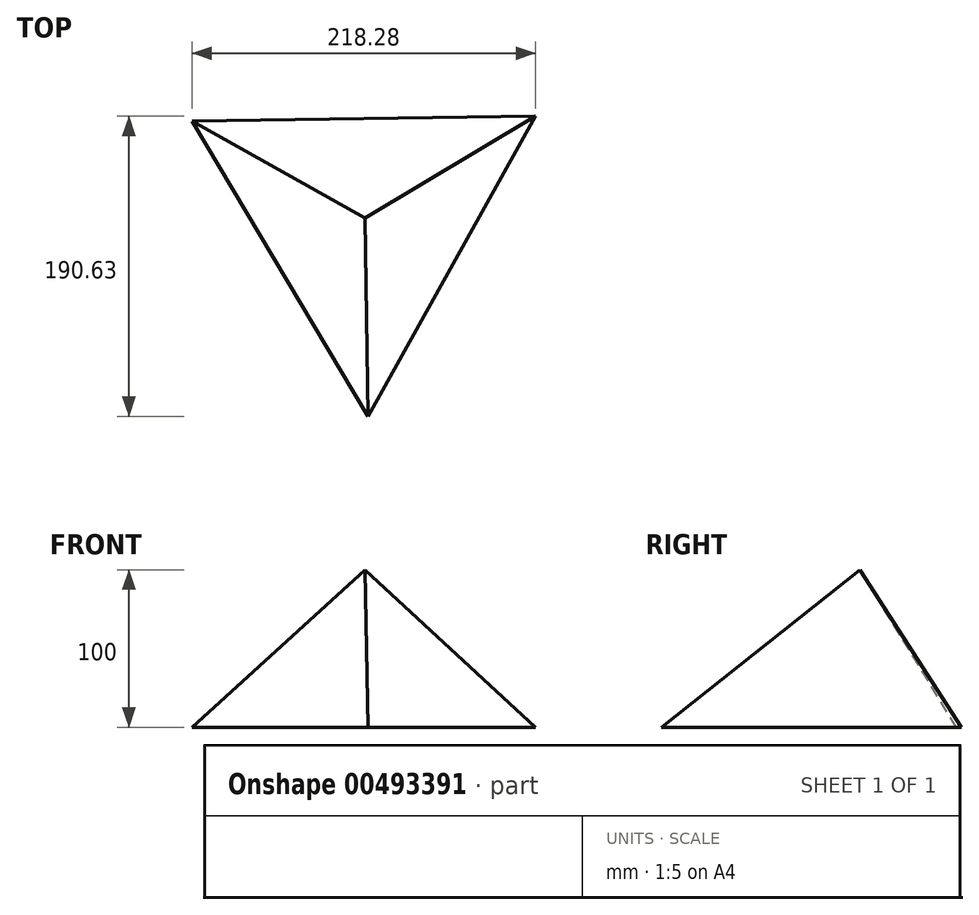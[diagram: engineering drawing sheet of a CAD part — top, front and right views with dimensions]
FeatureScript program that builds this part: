
annotation { "Feature Type Name" : "Feature", "Feature Type Description" : "" }
export const myFeature = defineFeature(function(context is Context, id is Id, definition is map)
    precondition{}
    {
        {
            var Q0;
            Q0=qCreatedBy(makeId("Top.planeOp"),FACE);
            var sketch = newSketch(context, id + "F0", { "sketchPlane" : qUnion([Q0])});
            skCircle(sketch, "E0.cCircle", {"center": v(0, 0) * mm, "radius": 126.04 * mm, "construction": true});
            skLineSegment(sketch, "E0.0", {"start": v(-110.06, 61.42) * mm, "end": v(108.22, 64.6) * mm});
            skLineSegment(sketch, "E0.1", {"start": v(108.22, 64.6) * mm, "end": v(1.84, -126.03) * mm});
            skLineSegment(sketch, "E0.2", {"start": v(1.84, -126.03) * mm, "end": v(-110.06, 61.42) * mm});
            skSolve(sketch);
        }
        {
            var Q0;
            Q0=qCreatedBy(makeId("Top.planeOp"),FACE);
            cPlane(context, id + "F1", {"entities" : qUnion([Q0]), "cplaneType" : CPlaneType.OFFSET, "offset" : 100 * mm, "width" : 150 * mm, "height" : 150 * mm});
        }
        {
            var Q0;
            Q0=qCreatedBy(id+"F1.planeOp",FACE);
            var sketch = newSketch(context, id + "F2", { "sketchPlane" : qUnion([Q0])});
            skPoint(sketch, "E1", {"position": v(0, 0) * mm});
            skSolve(sketch);
        }
        {
            var Q0;
            Q0=makeQuery(id+"F0.imprint","IMPRINT",FACE,{"disambiguationData":[TD([[makeQuery(id+"F0.imprint","IMPRINT",EDGE,{"derivedFrom":sQuery(id+"F0.wireOp",EDGE,"E0.0")}),-1.0]])]});
            var Q1;
            Q1=sQuery(id+"F2.wireOp",VERTEX,"E1");
            loft(context, id + "F3", {"sheetProfilesArray" : [{ "sheetProfileEntities" : qUnion([Q0]) }, { "sheetProfileEntities" : qUnion([Q1]) }]});
        }
    });
